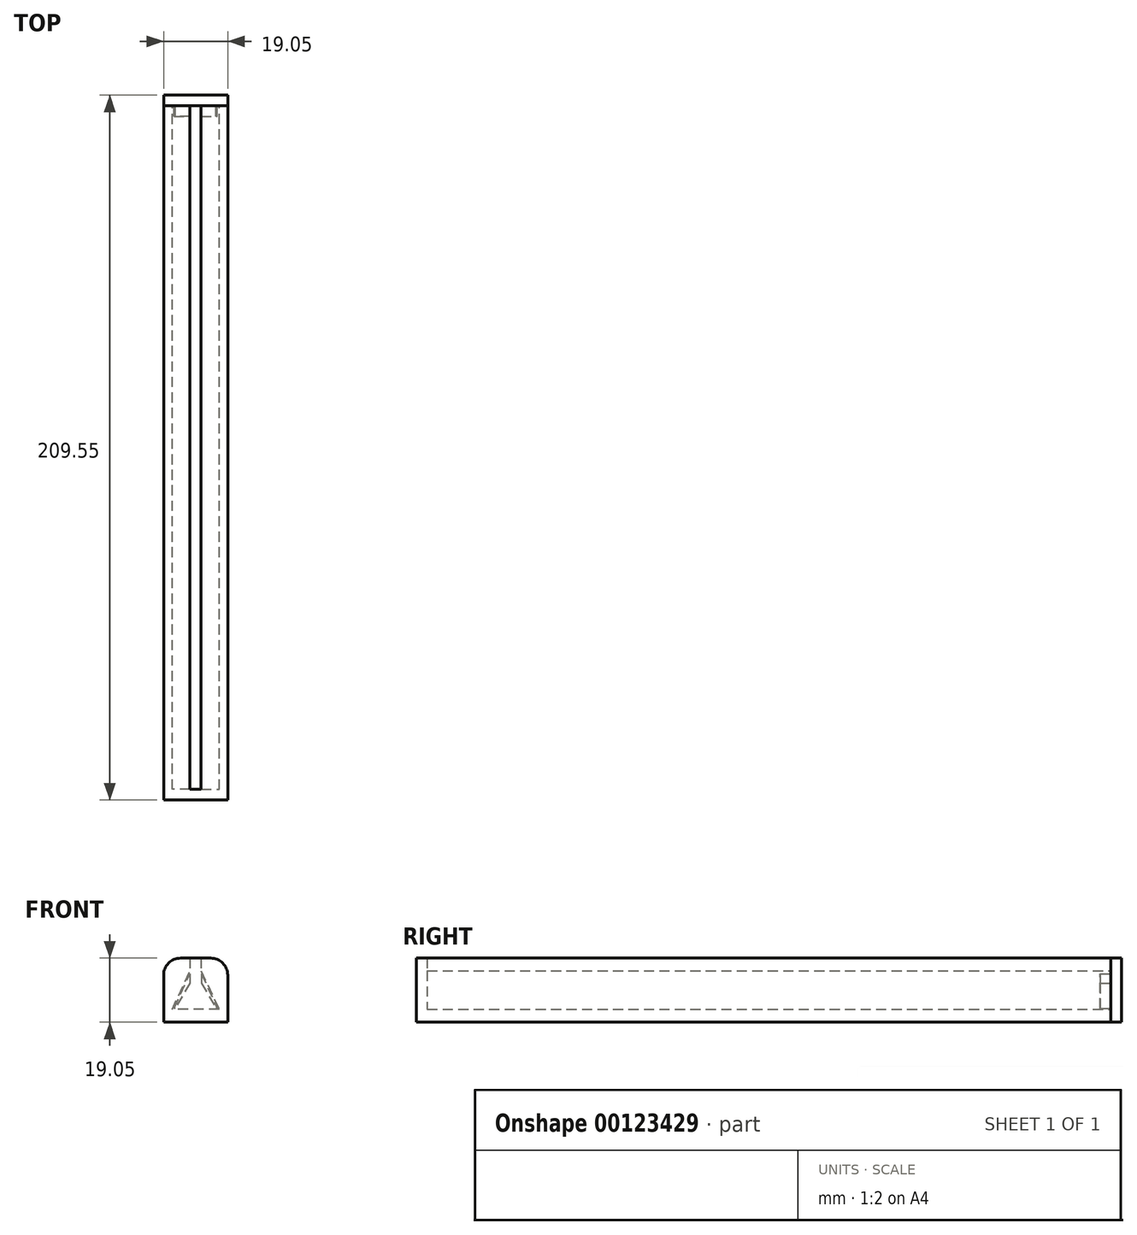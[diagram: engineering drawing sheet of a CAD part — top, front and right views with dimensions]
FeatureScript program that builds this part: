
annotation { "Feature Type Name" : "Feature", "Feature Type Description" : "" }
export const myFeature = defineFeature(function(context is Context, id is Id, definition is map)
    precondition{}
    {
        {
            var Q0;
            Q0=qCreatedBy(makeId("Front.planeOp"),FACE);
            var sketch = newSketch(context, id + "F0", { "sketchPlane" : qUnion([Q0])});
            skLineSegment(sketch, "E0.bottom", {"start": v(-45.22, 27.06) * mm, "end": v(-37.35, 27.06) * mm});
            skLineSegment(sketch, "E0.top", {"start": v(-45.22, 8.01) * mm, "end": v(-26.17, 8.01) * mm});
            skLineSegment(sketch, "E0.left", {"start": v(-45.22, 27.06) * mm, "end": v(-45.22, 8.01) * mm});
            skLineSegment(sketch, "E0.right", {"start": v(-26.17, 27.06) * mm, "end": v(-26.17, 8.01) * mm});
            skLineSegment(sketch, "E1", {"start": v(-35.7, 27.06) * mm, "end": v(-35.7, 8.01) * mm, "construction": true});
            skLineSegment(sketch, "E2", {"start": v(-28.71, 11.82) * mm, "end": v(-42.68, 11.82) * mm});
            skLineSegment(sketch, "E3.trimOffspring", {"start": v(-34.05, 27.06) * mm, "end": v(-26.17, 27.06) * mm});
            skLineSegment(sketch, "E4", {"start": v(-37.35, 27.06) * mm, "end": v(-37.35, 23.24) * mm});
            skLineSegment(sketch, "E5", {"start": v(-34.05, 27.06) * mm, "end": v(-34.05, 23.24) * mm});
            skLineSegment(sketch, "E6", {"start": v(-34.05, 23.24) * mm, "end": v(-28.71, 11.82) * mm});
            skLineSegment(sketch, "E7", {"start": v(-42.68, 11.82) * mm, "end": v(-37.35, 23.24) * mm});
            skSolve(sketch);
        }
        {
            var Q0;
            Q0=makeQuery(id+"F0.imprint","IMPRINT",FACE,{"disambiguationData":[TD([[makeQuery(id+"F0.imprint","IMPRINT",EDGE,{"derivedFrom":sQuery(id+"F0.wireOp",EDGE,"E0.bottom")}),-1.0]])]});
            extrude(context, id + "F1", {"entities" : qUnion([Q0]), "depth" : 203.2 * mm});
        }
        {
            var Q0;
            Q0=makeQuery(id+"F1.opExtrude","CAP_FACE",FACE,{"disambiguationData":[OSD([sQuery(id+"F0.wireOp",EDGE,"E0.bottom"),sQuery(id+"F0.wireOp",EDGE,"E0.top"),sQuery(id+"F0.wireOp",EDGE,"E0.left"),sQuery(id+"F0.wireOp",EDGE,"E0.right"),sQuery(id+"F0.wireOp",EDGE,"E2"),sQuery(id+"F0.wireOp",EDGE,"E3.trimOffspring"),sQuery(id+"F0.wireOp",EDGE,"E4"),sQuery(id+"F0.wireOp",EDGE,"E5"),sQuery(id+"F0.wireOp",EDGE,"E6"),sQuery(id+"F0.wireOp",EDGE,"E7")])],"isStart":false});
            var sketch = newSketch(context, id + "F2", { "sketchPlane" : qUnion([Q0])});
            skLineSegment(sketch, "E8.0", {"start": v(-26.17, 27.06) * mm, "end": v(-26.17, 8.01) * mm});
            skLineSegment(sketch, "E8.1", {"start": v(-45.22, 27.06) * mm, "end": v(-45.22, 8.01) * mm});
            skLineSegment(sketch, "E8.4", {"start": v(-45.22, 8.01) * mm, "end": v(-26.17, 8.01) * mm});
            skLineSegment(sketch, "E9", {"start": v(-45.22, 27.06) * mm, "end": v(-26.17, 27.06) * mm});
            skSolve(sketch);
        }
        {
            var Q0;
            Q0 = qSketchRegion(id + "F2", true);
            extrude(context, id + "F3", {"entities" : qUnion([Q0]), "operationType" : NewBodyOperationType.ADD, "depth" : 3.17 * mm});
        }
        {
            var Q0;
            Q0=makeQuery(id+"F1.opExtrude","SWEPT_EDGE",EDGE,{"disambiguationData":[OSD([sQuery(id+"F0.wireOp",EDGE,"E0.bottom"),sQuery(id+"F0.wireOp",EDGE,"E0.left")])]});
            var Q1;
            Q1=makeQuery(id+"F1.opExtrude","SWEPT_EDGE",EDGE,{"disambiguationData":[OSD([sQuery(id+"F0.wireOp",EDGE,"E0.right"),sQuery(id+"F0.wireOp",EDGE,"E3.trimOffspring")])]});
            fillet(context, id + "F4", {"entities" : qUnion([Q0, Q1]), "radius" : 5.08 * mm, "tangentPropagation" : true, "allowEdgeOverflow" : false});
        }
        {
            var Q0;
            Q0=makeQuery(id+"F1.opExtrude","CAP_FACE",FACE,{"disambiguationData":[OSD([sQuery(id+"F0.wireOp",EDGE,"E0.bottom"),sQuery(id+"F0.wireOp",EDGE,"E0.top"),sQuery(id+"F0.wireOp",EDGE,"E0.left"),sQuery(id+"F0.wireOp",EDGE,"E0.right"),sQuery(id+"F0.wireOp",EDGE,"E2"),sQuery(id+"F0.wireOp",EDGE,"E3.trimOffspring"),sQuery(id+"F0.wireOp",EDGE,"E4"),sQuery(id+"F0.wireOp",EDGE,"E5"),sQuery(id+"F0.wireOp",EDGE,"E6"),sQuery(id+"F0.wireOp",EDGE,"E7")])],"isStart":true});
            var sketch = newSketch(context, id + "F5", { "sketchPlane" : qUnion([Q0])});
            skLineSegment(sketch, "E10.0", {"start": v(28.71, 11.82) * mm, "end": v(42.68, 11.82) * mm});
            skLineSegment(sketch, "E10.1", {"start": v(42.68, 11.82) * mm, "end": v(37.35, 23.24) * mm});
            skLineSegment(sketch, "E10.2", {"start": v(34.05, 23.24) * mm, "end": v(28.71, 11.82) * mm});
            skArc(sketch, "E10.3", {"start": v(31.25, 27.06) * mm, "mid": v(27.66, 25.57) * mm, "end": v(26.17, 21.98) * mm});
            skLineSegment(sketch, "E10.4", {"start": v(34.05, 27.06) * mm, "end": v(31.25, 27.06) * mm});
            skLineSegment(sketch, "E10.5", {"start": v(26.17, 21.98) * mm, "end": v(26.17, 8.01) * mm});
            skLineSegment(sketch, "E10.6", {"start": v(40.14, 27.06) * mm, "end": v(37.35, 27.06) * mm});
            skArc(sketch, "E10.7", {"start": v(45.22, 21.98) * mm, "mid": v(43.73, 25.57) * mm, "end": v(40.14, 27.06) * mm});
            skLineSegment(sketch, "E10.8", {"start": v(45.22, 21.98) * mm, "end": v(45.22, 8.01) * mm});
            skLineSegment(sketch, "E10.9", {"start": v(45.22, 8.01) * mm, "end": v(26.17, 8.01) * mm});
            skLineSegment(sketch, "E11", {"start": v(34.05, 23.24) * mm, "end": v(37.35, 23.24) * mm});
            skLineSegment(sketch, "E12", {"start": v(34.05, 27.06) * mm, "end": v(37.35, 27.06) * mm});
            skSolve(sketch);
        }
        {
            var Q0;
            Q0=makeQuery(id+"F5.imprint","IMPRINT",FACE,{"disambiguationData":[TD([[makeQuery(id+"F5.imprint","IMPRINT",EDGE,{"derivedFrom":sQuery(id+"F5.wireOp",EDGE,"E10.0")}),-1.0]])]});
            var Q1;
            Q1=makeQuery(id+"F5.imprint","IMPRINT",FACE,{"disambiguationData":[TD([[makeQuery(id+"F5.imprint","IMPRINT",EDGE,{"derivedFrom":sQuery(id+"F5.wireOp",EDGE,"E10.0")}),1.0]])]});
            var Q2;
            Q2=makeQuery(id+"F5.imprint","IMPRINT",FACE,{"disambiguationData":[TD([[makeQuery(id+"F5.imprint","IMPRINT",EDGE,{"derivedFrom":sQuery(id+"F5.wireOp",EDGE,"E11")}),1.0]])]});
            extrude(context, id + "F6", {"entities" : qUnion([Q0, Q1, Q2]), "depth" : 3.17 * mm});
        }
        {
            var Q0;
            Q0=makeQuery(id+"F6.opExtrude","CAP_FACE",FACE,{"disambiguationData":[OSD([sQuery(id+"F5.wireOp",EDGE,"E10.0"),sQuery(id+"F5.wireOp",EDGE,"E10.1"),sQuery(id+"F5.wireOp",EDGE,"E10.2"),sQuery(id+"F5.wireOp",EDGE,"E10.3"),sQuery(id+"F5.wireOp",EDGE,"E10.4"),sQuery(id+"F5.wireOp",EDGE,"E10.5"),sQuery(id+"F5.wireOp",EDGE,"E10.6"),sQuery(id+"F5.wireOp",EDGE,"E10.7"),sQuery(id+"F5.wireOp",EDGE,"E10.8"),sQuery(id+"F5.wireOp",EDGE,"E10.9"),sQuery(id+"F5.wireOp",EDGE,"E11"),sQuery(id+"F5.wireOp",EDGE,"E12")])],"isStart":false});
            var sketch = newSketch(context, id + "F7", { "sketchPlane" : qUnion([Q0])});
            skLineSegment(sketch, "E13.0", {"start": v(42.68, 11.82) * mm, "end": v(37.35, 23.04) * mm, "construction": true});
            skLineSegment(sketch, "E13.2", {"start": v(34.05, 23.24) * mm, "end": v(28.71, 11.82) * mm, "construction": true});
            skLineSegment(sketch, "E13.3", {"start": v(28.71, 11.82) * mm, "end": v(42.68, 11.82) * mm, "construction": true});
            skLineSegment(sketch, "E14.0", {"start": v(29.25, 12.16) * mm, "end": v(42.14, 12.16) * mm});
            skLineSegment(sketch, "E15.trimOffspring", {"start": v(42.14, 12.16) * mm, "end": v(37.13, 22.9) * mm});
            skLineSegment(sketch, "E16.trimOffspring", {"start": v(34.26, 22.9) * mm, "end": v(29.25, 12.16) * mm});
            skLineSegment(sketch, "E17.trimOffspring", {"start": v(34.26, 22.9) * mm, "end": v(37.13, 22.9) * mm});
            skLineSegment(sketch, "E18", {"start": v(37.35, 23.04) * mm, "end": v(37.35, 19.62) * mm});
            skLineSegment(sketch, "E19", {"start": v(37.35, 19.62) * mm, "end": v(41.78, 12.16) * mm});
            skLineSegment(sketch, "E20", {"start": v(35.7, 12.16) * mm, "end": v(35.7, 19.86) * mm, "construction": true});
            skLineSegment(sketch, "E21.MirrorCS", {"start": v(34.04, 23.04) * mm, "end": v(34.04, 19.62) * mm});
            skLineSegment(sketch, "E22.MirrorCS", {"start": v(34.04, 19.62) * mm, "end": v(29.62, 12.16) * mm});
            skSolve(sketch);
        }
        {
            var Q0;
            {var subQ3=sQuery(id+"F7.wireOp",EDGE,"E19");Q0=makeQuery(id+"F7.imprint","IMPRINT",FACE,{"disambiguationData":[TD([[makeQuery(id+"F7.imprint","IMPRINT",EDGE,{"derivedFrom":subQ3}),1.0]])]});}
            var Q1;
            {var subQ3=sQuery(id+"F7.wireOp",EDGE,"E22.MirrorCS");Q1=makeQuery(id+"F7.imprint","IMPRINT",FACE,{"disambiguationData":[TD([[makeQuery(id+"F7.imprint","IMPRINT",EDGE,{"derivedFrom":subQ3}),-1.0]])]});}
            extrude(context, id + "F8", {"entities" : qUnion([Q0, Q1]), "operationType" : NewBodyOperationType.ADD, "oppositeDirection" : true, "depth" : 6.35 * mm});
        }
    });
